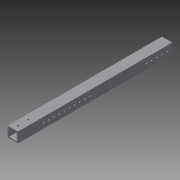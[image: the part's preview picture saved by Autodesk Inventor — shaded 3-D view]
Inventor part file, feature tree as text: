
AUTODESK INVENTOR PART (.ipt)
format: ipt  version: 2014 (Build 180170000, 170)  size: 139,264 bytes
history: native  units: in
note: dims shown in document units (in); Inventor stores cm internally (conversion verified against a paired STEP export)
features: extrude x3, sketch x3
ambient origin geometry x8: Origin, YZ Plane, XZ Plane, XY Plane, X Axis, Y Axis, Z Axis, Center Point
bodies: Solid1 (feature_tree)
feature tree (6):
  extrude  "Extrusion1"  Depth=1.0in
  extrude  "Extrusion2"  Depth=15.0in TaperAngle=0.0deg
  extrude  "Extrusion3"  Depth=15.0in
  sketch  "Sketch1"  dims[d0=1.0in d1=1.0in]
  sketch  "Sketch2"  dims[d2=0.125in d3=15.0in d4=0.0in]
  sketch  "Sketch3"  dims[d5=0.163in d6=0.5in d7=2.5in d8=3.937in d10=0.5in d11=0.3937in d13=1.0in d15=0.5in d16=0.5in d17=1.9685in d19=0.5in d20=0.3937in d22=1.0in d24=15.0in d25=0.0in d26=0.163in d27=0.5in d28=0.5in d29=0.7874in d31=1.0in d32=0.3937in d34=1.0in d36=15.0in d37=0.0in]
